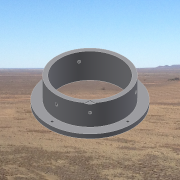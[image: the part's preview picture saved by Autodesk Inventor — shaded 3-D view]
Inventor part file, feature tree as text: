
AUTODESK INVENTOR PART (.ipt)
format: ipt  version: 2014 SP1 (Build 180222100, 222)  size: 194,048 bytes
history: native  units: in
note: dims shown in document units (in); Inventor stores cm internally (conversion verified against a paired STEP export)
features: sketch x7, hole x4, extrude x3, plane x3, pattern_circular x2
ambient origin geometry x8: Origin, YZ Plane, XZ Plane, XY Plane, X Axis, Y Axis, Z Axis, Center Point
bodies: Solid1 (feature_tree)
feature tree (19):
  extrude  "Extrusion1"  Depth=1.5in TaperAngle=0.0deg
  hole  "centralHole"  [1 undecoded]
  extrude  "Extrusion2"  Depth=2.25in
  hole  "Hole2"  [1 undecoded]
  pattern_circular  "Circular Pattern1"  Count=3 Angle=360.0deg
  plane  "Work Plane1"
  hole  "Hole3"  [1 undecoded]
  pattern_circular  "Circular Pattern2"  [2 undecoded]
  plane  "Work Plane3"
  hole  "Hole4"  [1 undecoded]
  extrude  "Extrusion3"  Depth=0.06in TaperAngle=0.0deg
  sketch  "Sketch1"  dims[d0=5.0in d1=1.5in d2=0.0in]
  sketch  "Sketch2"  dims[d3=3.55in]
  sketch  "Sketch3"  dims[d4=3.55in d5=0.75in d6=0.375in d7=0.25in d8=0.5635in d9=1.0in d10=0.8108in d11=4.0in]
  sketch  "Sketch4"  dims[d12=1.25in d13=0.0in d14=2.25in]
  sketch  "Sketch5"  dims[d15=0.15in d16=0.75in d17=0.375in d18=0.25in d19=0.5635in d20=1.0in d21=0.8108in d22=1.5748in d23=360.0deg]
  plane  "Work Plane2"
  sketch  "Sketch6"  dims[d25=2.0in]
  sketch  "Sketch7"  dims[d26=0.5in d27=0.156in d28=0.75in d29=0.375in d30=0.25in d31=0.5635in d32=1.0in d33=0.8108in d34=1.1811in d35=360.0deg d37=45.0deg d38=2.0in d39=0.5in d40=0.156in d41=0.75in d42=0.375in d43=0.25in d44=0.5635in d45=1.0in d46=0.8108in d47=45.0deg d48=0.06in d49=0.0in]
note: 6 required parameter values undecoded (feature->parameter linkage not recoverable at this tier; creation-order binding heuristic only, values carry confidence <= 0.55)
